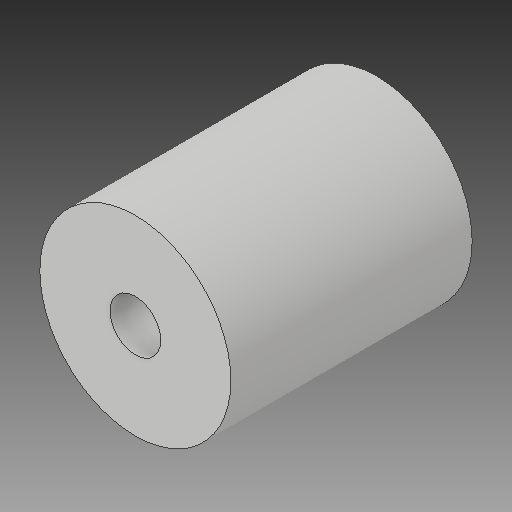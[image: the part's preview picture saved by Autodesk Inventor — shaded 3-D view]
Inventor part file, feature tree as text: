
AUTODESK INVENTOR PART (.ipt)
format: ipt  version: 2019 (Build 230136000, 136)  size: 97,280 bytes
history: native  units: mm
features: other x3, sketch x1
ambient origin geometry x8: Origin, YZ Plane, XZ Plane, XY Plane, X Axis, Y Axis, Z Axis, Center Point
bodies: Solid1 (feature_tree)
feature tree (4):
  other  "Flex_link_5mm.ipt"
  other  "Solid1::Flex_link_5mm.ipt"
  other  "TaggingFeature1"
  sketch  "Sketch1"  dims[d0=10.0mm]
